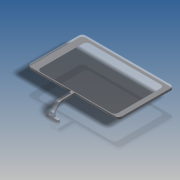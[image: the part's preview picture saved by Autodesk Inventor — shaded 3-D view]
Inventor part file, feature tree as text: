
AUTODESK INVENTOR PART (.ipt)
format: ipt  version: 2016 SP2 (Build 200236200, 236)  size: 227,328 bytes
history: native  units: in
note: dims shown in document units (in); Inventor stores cm internally (conversion verified against a paired STEP export)
features: extrude x4, other x2, sketch x2, fillet x1
ambient origin geometry x8: Origin, YZ Plane, XZ Plane, XY Plane, X Axis, Y Axis, Z Axis, Center Point
bodies: Body1 (feature_tree), Body2 (feature_tree)
feature tree (9):
  other  "Black"
  other  "Lens"
  sketch  "Sketch2"  dims[d0=1.2283in d1=2.0472in]
  extrude  "Extrusion1"  Depth=2.0472in
  sketch  "Sketch3"  dims[d2=0.0787in d3=1.1024in d4=1.7323in d5=0.0787in d6=0.0472in d7=0.0in d8=0.0in d9=0.0in d10=0.2677in d11=0.1575in d12=0.0472in d13=0.063in d14=0.4724in d15=0.315in d16=0.2677in d17=0.1417in d18=0.0787in d19=0.0in d20=0.2677in d21=0.0in d22=0.0787in d23=0.315in d24=0.0039in]
  extrude  "Extrusion3"  Depth=1.1024in
  extrude  "Extrusion4"  Depth=1.7323in
  extrude  "Extrusion2"  Depth=0.0787in
  fillet  "Fillet1"  Radius=0.0472in
